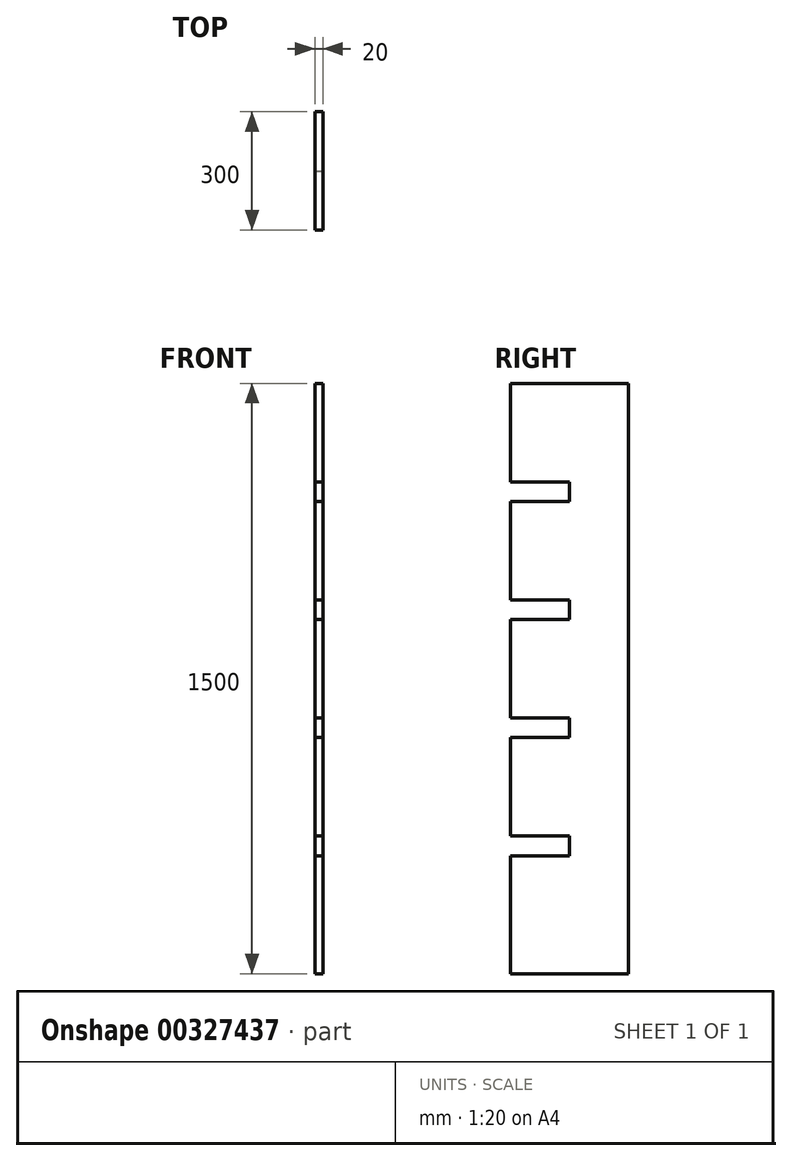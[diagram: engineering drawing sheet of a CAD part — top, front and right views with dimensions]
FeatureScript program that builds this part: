
annotation { "Feature Type Name" : "Feature", "Feature Type Description" : "" }
export const myFeature = defineFeature(function(context is Context, id is Id, definition is map)
    precondition{}
    {
        {
            var Q0;
            Q0=qCreatedBy(makeId("Front.planeOp"),FACE);
            var sketch = newSketch(context, id + "F0", { "sketchPlane" : qUnion([Q0])});
            skLineSegment(sketch, "E0", {"start": v(-57.01, 775.25) * mm, "end": v(-57.01, -724.75) * mm});
            skLineSegment(sketch, "E1", {"start": v(-57.01, -724.75) * mm, "end": v(-37.01, -724.75) * mm});
            skLineSegment(sketch, "E2", {"start": v(-57.01, 775.25) * mm, "end": v(-37.01, 775.25) * mm});
            skLineSegment(sketch, "E3", {"start": v(-37.01, 775.25) * mm, "end": v(-37.01, -724.75) * mm});
            skPoint(sketch, "E4.MirrorCS.end.orphan", {"position": v(-37.01, 175.25) * mm});
            skSolve(sketch);
        }
        {
            var Q0;
            Q0 = qSketchRegion(id + "F0", true);
            extrude(context, id + "F1", {"entities" : qUnion([Q0]), "depth" : 300 * mm});
        }
        {
            var Q0;
            Q0=makeQuery(id+"F1.opExtrude","SWEPT_FACE",FACE,{"disambiguationData":[OSD([sQuery(id+"F0.wireOp",EDGE,"E3")])]});
            var sketch = newSketch(context, id + "F2", { "sketchPlane" : qUnion([Q0])});
            skLineSegment(sketch, "E5", {"start": v(-300, 525.25) * mm, "end": v(0, 525.25) * mm});
            skLineSegment(sketch, "E6", {"start": v(-300, 475.25) * mm, "end": v(0, 475.25) * mm});
            skLineSegment(sketch, "E7", {"start": v(-300, 225.25) * mm, "end": v(0, 225.25) * mm});
            skLineSegment(sketch, "E8", {"start": v(-300, 175.25) * mm, "end": v(0, 175.25) * mm});
            skLineSegment(sketch, "E9", {"start": v(-300, -74.75) * mm, "end": v(0, -74.75) * mm});
            skLineSegment(sketch, "E10", {"start": v(-300, -124.75) * mm, "end": v(0, -124.75) * mm});
            skLineSegment(sketch, "E11", {"start": v(-300, -374.75) * mm, "end": v(0, -374.75) * mm});
            skLineSegment(sketch, "E12", {"start": v(-300, -424.75) * mm, "end": v(0, -424.75) * mm});
            skLineSegment(sketch, "E13", {"start": v(-150, 775.25) * mm, "end": v(-150, -724.75) * mm});
            skSolve(sketch);
        }
        {
            var Q0;
            {var subQ0=sQuery(id+"F2.wireOp",EDGE,"E5");var subQ1=makeQuery(id+"F1.opExtrude","CAP_EDGE",EDGE,{"disambiguationData":[OSD([sQuery(id+"F0.wireOp",EDGE,"E3")])],"isStart":false});var subQ2=makeQuery(id+"F2.imprint","INTERSECT",VERTEX,{"derivedFrom":[subQ1,subQ0]});Q0=makeQuery(id+"F2.imprint","IMPRINT",FACE,{"disambiguationData":[TD([[makeQuery(id+"F2.imprint","IMPRINT",EDGE,{"disambiguationData":[TD([[subQ2,-1.0]])],"derivedFrom":subQ0}),-1.0]])]});}
            var Q1;
            {var subQ0=sQuery(id+"F2.wireOp",EDGE,"E7");var subQ1=makeQuery(id+"F1.opExtrude","CAP_EDGE",EDGE,{"disambiguationData":[OSD([sQuery(id+"F0.wireOp",EDGE,"E3")])],"isStart":false});var subQ2=makeQuery(id+"F2.imprint","INTERSECT",VERTEX,{"derivedFrom":[subQ1,subQ0]});Q1=makeQuery(id+"F2.imprint","IMPRINT",FACE,{"disambiguationData":[TD([[makeQuery(id+"F2.imprint","IMPRINT",EDGE,{"disambiguationData":[TD([[subQ2,-1.0]])],"derivedFrom":subQ0}),-1.0]])]});}
            var Q2;
            {var subQ0=sQuery(id+"F2.wireOp",EDGE,"E9");var subQ1=makeQuery(id+"F1.opExtrude","CAP_EDGE",EDGE,{"disambiguationData":[OSD([sQuery(id+"F0.wireOp",EDGE,"E3")])],"isStart":false});var subQ2=makeQuery(id+"F2.imprint","INTERSECT",VERTEX,{"derivedFrom":[subQ1,subQ0]});Q2=makeQuery(id+"F2.imprint","IMPRINT",FACE,{"disambiguationData":[TD([[makeQuery(id+"F2.imprint","IMPRINT",EDGE,{"disambiguationData":[TD([[subQ2,-1.0]])],"derivedFrom":subQ0}),-1.0]])]});}
            var Q3;
            {var subQ0=sQuery(id+"F2.wireOp",EDGE,"E11");var subQ1=makeQuery(id+"F1.opExtrude","CAP_EDGE",EDGE,{"disambiguationData":[OSD([sQuery(id+"F0.wireOp",EDGE,"E3")])],"isStart":false});var subQ2=makeQuery(id+"F2.imprint","INTERSECT",VERTEX,{"derivedFrom":[subQ1,subQ0]});Q3=makeQuery(id+"F2.imprint","IMPRINT",FACE,{"disambiguationData":[TD([[makeQuery(id+"F2.imprint","IMPRINT",EDGE,{"disambiguationData":[TD([[subQ2,-1.0]])],"derivedFrom":subQ0}),-1.0]])]});}
            extrude(context, id + "F3", {"entities" : qUnion([Q0, Q1, Q2, Q3]), "operationType" : NewBodyOperationType.REMOVE, "oppositeDirection" : true, "depth" : 20 * mm});
        }
    });
